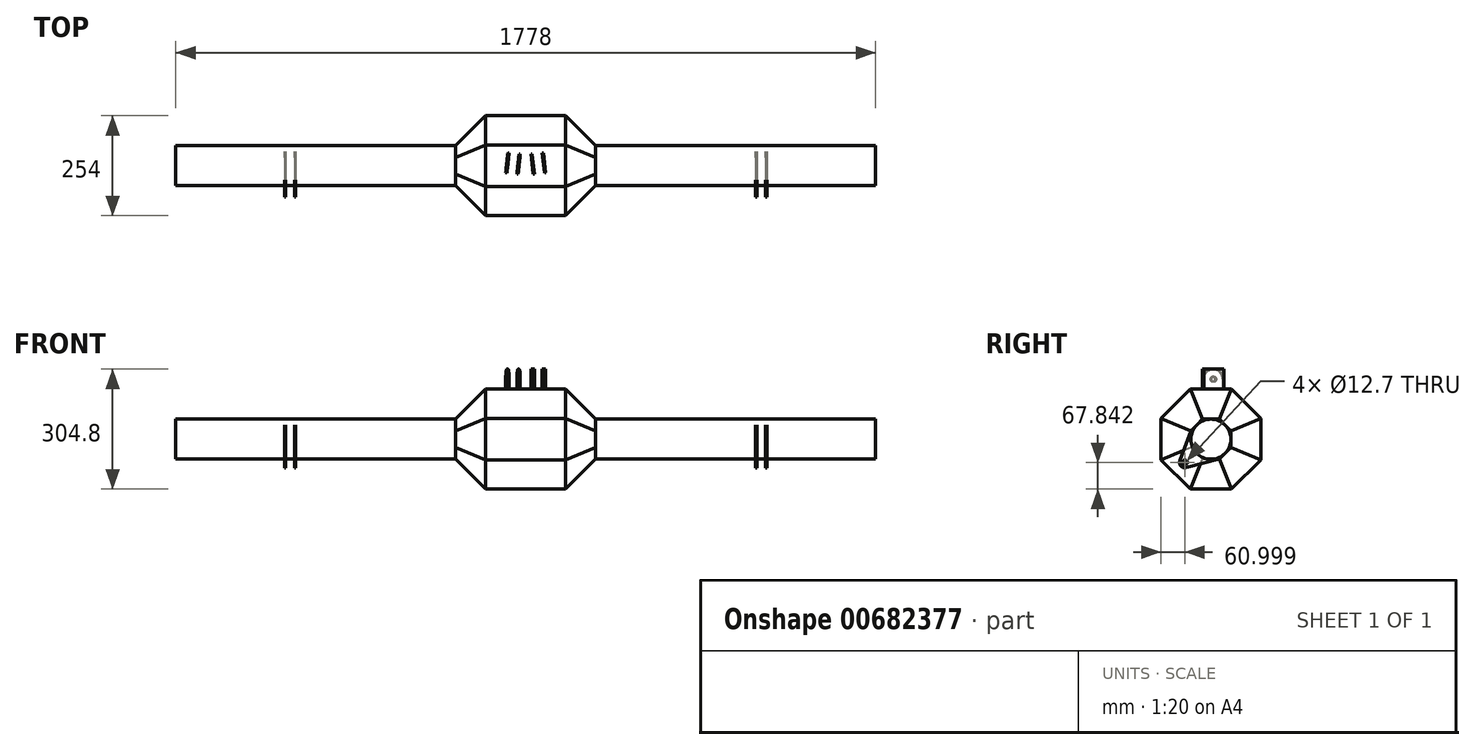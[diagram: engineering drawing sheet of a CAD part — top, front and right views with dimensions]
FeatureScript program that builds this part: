
annotation { "Feature Type Name" : "Feature", "Feature Type Description" : "" }
export const myFeature = defineFeature(function(context is Context, id is Id, definition is map)
    precondition{}
    {
        {
            var Q0;
            Q0=qCreatedBy(makeId("Right.planeOp"),FACE);
            var sketch = newSketch(context, id + "F0", { "sketchPlane" : qUnion([Q0])});
            skCircle(sketch, "E0", {"center": v(0, 0) * mm, "radius": 50.8 * mm});
            skSolve(sketch);
        }
        {
            var Q0;
            Q0=makeQuery(id+"F0.imprint","IMPRINT",FACE,{"disambiguationData":[TD([[makeQuery(id+"F0.imprint","IMPRINT",EDGE,{"derivedFrom":sQuery(id+"F0.wireOp",EDGE,"E0")}),1.0]])]});
            extrude(context, id + "F1", {"entities" : qUnion([Q0]), "endBound" : BoundingType.SYMMETRIC, "depth" : 1778 * mm, "offsetDistance" : 25.4 * mm});
        }
        {
            var Q0;
            Q0=qCreatedBy(makeId("Right.planeOp"),FACE);
            var sketch = newSketch(context, id + "F2", { "sketchPlane" : qUnion([Q0])});
            skCircle(sketch, "E1.cCircle", {"center": v(0, 0) * mm, "radius": 127 * mm, "construction": true});
            skLineSegment(sketch, "E1.0", {"start": v(52.6, 127) * mm, "end": v(127, 52.6) * mm});
            skLineSegment(sketch, "E1.1", {"start": v(127, 52.6) * mm, "end": v(127, -52.6) * mm});
            skLineSegment(sketch, "E1.2", {"start": v(127, -52.6) * mm, "end": v(52.6, -127) * mm});
            skLineSegment(sketch, "E1.3", {"start": v(52.6, -127) * mm, "end": v(-52.6, -127) * mm});
            skLineSegment(sketch, "E1.4", {"start": v(-52.6, -127) * mm, "end": v(-127, -52.6) * mm});
            skLineSegment(sketch, "E1.5", {"start": v(-127, -52.6) * mm, "end": v(-127, 52.6) * mm});
            skLineSegment(sketch, "E1.6", {"start": v(-127, 52.6) * mm, "end": v(-52.6, 127) * mm});
            skLineSegment(sketch, "E1.7", {"start": v(-52.6, 127) * mm, "end": v(52.6, 127) * mm});
            skPoint(sketch, "E1.0.midPoint", {"position": v(89.8, 89.8) * mm});
            skSolve(sketch);
        }
        {
            var Q0;
            Q0=makeQuery(id+"F2.imprint","IMPRINT",FACE,{"disambiguationData":[TD([[makeQuery(id+"F2.imprint","IMPRINT",EDGE,{"derivedFrom":sQuery(id+"F2.wireOp",EDGE,"E1.0")}),-1.0]])]});
            extrude(context, id + "F3", {"entities" : qUnion([Q0]), "operationType" : NewBodyOperationType.ADD, "endBound" : BoundingType.SYMMETRIC, "depth" : 355.6 * mm, "offsetDistance" : 25.4 * mm});
        }
        {
            var Q0;
            Q0=makeQuery(id+"F3.opExtrude","CAP_EDGE",EDGE,{"disambiguationData":[OSD([sQuery(id+"F2.wireOp",EDGE,"E1.5")])],"isStart":true});
            var Q1;
            Q1=makeQuery(id+"F3.opExtrude","CAP_EDGE",EDGE,{"disambiguationData":[OSD([sQuery(id+"F2.wireOp",EDGE,"E1.6")])],"isStart":true});
            var Q2;
            Q2=makeQuery(id+"F3.opExtrude","CAP_EDGE",EDGE,{"disambiguationData":[OSD([sQuery(id+"F2.wireOp",EDGE,"E1.7")])],"isStart":true});
            var Q3;
            Q3=makeQuery(id+"F3.opExtrude","CAP_EDGE",EDGE,{"disambiguationData":[OSD([sQuery(id+"F2.wireOp",EDGE,"E1.0")])],"isStart":true});
            var Q4;
            Q4=makeQuery(id+"F3.opExtrude","CAP_EDGE",EDGE,{"disambiguationData":[OSD([sQuery(id+"F2.wireOp",EDGE,"E1.1")])],"isStart":true});
            var Q5;
            Q5=makeQuery(id+"F3.opExtrude","CAP_EDGE",EDGE,{"disambiguationData":[OSD([sQuery(id+"F2.wireOp",EDGE,"E1.2")])],"isStart":true});
            var Q6;
            Q6=makeQuery(id+"F3.opExtrude","CAP_EDGE",EDGE,{"disambiguationData":[OSD([sQuery(id+"F2.wireOp",EDGE,"E1.3")])],"isStart":true});
            var Q7;
            Q7=makeQuery(id+"F3.opExtrude","CAP_EDGE",EDGE,{"disambiguationData":[OSD([sQuery(id+"F2.wireOp",EDGE,"E1.4")])],"isStart":true});
            chamfer(context, id + "F4", {"entities" : qUnion([Q0, Q1, Q2, Q3, Q4, Q5, Q6, Q7]), "width" : 76.2 * mm, "tangentPropagation" : true});
        }
        {
            var Q0;
            Q0=makeQuery(id+"F3.opExtrude","CAP_EDGE",EDGE,{"disambiguationData":[OSD([sQuery(id+"F2.wireOp",EDGE,"E1.0")])],"isStart":false});
            var Q1;
            Q1=makeQuery(id+"F3.opExtrude","CAP_EDGE",EDGE,{"disambiguationData":[OSD([sQuery(id+"F2.wireOp",EDGE,"E1.6")])],"isStart":false});
            var Q2;
            Q2=makeQuery(id+"F3.opExtrude","CAP_EDGE",EDGE,{"disambiguationData":[OSD([sQuery(id+"F2.wireOp",EDGE,"E1.7")])],"isStart":false});
            var Q3;
            Q3=makeQuery(id+"F3.opExtrude","CAP_EDGE",EDGE,{"disambiguationData":[OSD([sQuery(id+"F2.wireOp",EDGE,"E1.5")])],"isStart":false});
            var Q4;
            Q4=makeQuery(id+"F3.opExtrude","CAP_EDGE",EDGE,{"disambiguationData":[OSD([sQuery(id+"F2.wireOp",EDGE,"E1.4")])],"isStart":false});
            var Q5;
            Q5=makeQuery(id+"F3.opExtrude","CAP_EDGE",EDGE,{"disambiguationData":[OSD([sQuery(id+"F2.wireOp",EDGE,"E1.3")])],"isStart":false});
            var Q6;
            Q6=makeQuery(id+"F3.opExtrude","CAP_EDGE",EDGE,{"disambiguationData":[OSD([sQuery(id+"F2.wireOp",EDGE,"E1.2")])],"isStart":false});
            var Q7;
            Q7=makeQuery(id+"F3.opExtrude","CAP_EDGE",EDGE,{"disambiguationData":[OSD([sQuery(id+"F2.wireOp",EDGE,"E1.1")])],"isStart":false});
            chamfer(context, id + "F5", {"entities" : qUnion([Q0, Q1, Q2, Q3, Q4, Q5, Q6, Q7]), "width" : 76.2 * mm, "tangentPropagation" : true});
        }
        {
            var Q0;
            Q0=makeQuery(id+"F1.opExtrude","CAP_FACE",FACE,{"disambiguationData":[OSD([sQuery(id+"F0.wireOp",EDGE,"E0")])],"isStart":true});
            cPlane(context, id + "F6", {"entities" : qUnion([Q0]), "cplaneType" : CPlaneType.OFFSET, "offset" : 304.8 * mm, "oppositeDirection" : true, "width" : 152.4 * mm, "height" : 152.4 * mm});
        }
        {
            var Q0;
            Q0=qCreatedBy(id+"F6.planeOp",FACE);
            var sketch = newSketch(context, id + "F7", { "sketchPlane" : qUnion([Q0])});
            skCircle(sketch, "E2", {"center": v(66, -59.16) * mm, "radius": 6.35 * mm});
            skPoint(sketch, "E3", {"position": v(50.8, 21.04) * mm});
            skPoint(sketch, "E4", {"position": v(-21.04, -50.8) * mm});
            skLineSegment(sketch, "E5", {"start": v(62.22, -64.26) * mm, "end": v(66, -59.16) * mm});
            skLineSegment(sketch, "E6", {"start": v(69.78, -54.06) * mm, "end": v(66, -59.16) * mm});
            skCircle(sketch, "E7.0", {"center": v(0, 0) * mm, "radius": 50.8 * mm});
            skLineSegment(sketch, "E8", {"start": v(50.8, 21.04) * mm, "end": v(35.92, 35.92) * mm});
            skLineSegment(sketch, "E9", {"start": v(-21.04, -50.8) * mm, "end": v(-35.82, -36.03) * mm});
            skArc(sketch, "E10", {"start": v(62.57, -72.43) * mm, "mid": v(76.18, -68.34) * mm, "end": v(78.85, -54.38) * mm});
            skLineSegment(sketch, "E11", {"start": v(50.8, 21.04) * mm, "end": v(78.85, -54.38) * mm});
            skLineSegment(sketch, "E12", {"start": v(-21.04, -50.8) * mm, "end": v(62.57, -72.43) * mm});
            skSolve(sketch);
        }
        {
            var Q0;
            {var subQ0=sQuery(id+"F7.wireOp",EDGE,"E8");Q0=makeQuery(id+"F7.imprint","IMPRINT",FACE,{"disambiguationData":[TD([[makeQuery(id+"F7.imprint","IMPRINT",EDGE,{"derivedFrom":subQ0}),1.0]])]});}
            extrude(context, id + "F8", {"entities" : qUnion([Q0]), "depth" : 3.17 * mm, "offsetDistance" : 25.4 * mm});
        }
        {
            var Q0;
            Q0=makeQuery(id+"F8.opExtrude","SWEPT_BODY",BODY,{"disambiguationData":[OSD([sQuery(id+"F7.wireOp",EDGE,"E2"),sQuery(id+"F7.wireOp",EDGE,"E7.0"),sQuery(id+"F7.wireOp",EDGE,"E8"),sQuery(id+"F7.wireOp",EDGE,"E9"),sQuery(id+"F7.wireOp",EDGE,"E10"),sQuery(id+"F7.wireOp",EDGE,"E11"),sQuery(id+"F7.wireOp",EDGE,"E12")])]});
            var Q1;
            {var subQ0=sQuery(id+"F0.wireOp",EDGE,"E0");Q1=makeQuery(id+"F3.boolean.opBoolean","SPLIT",FACE,{"disambiguationData":[TD([makeQuery(id+"F1.opExtrude","CAP_FACE",FACE,{"disambiguationData":[OSD([subQ0])],"isStart":true})])],"derivedFrom":makeQuery(id+"F1.opExtrude","SWEPT_FACE",FACE,{"disambiguationData":[OSD([subQ0])]})});}
            transform(context, id + "F9", {"entities" : qUnion([Q0]), "transformType" : TransformType.TRANSLATION_DISTANCE, "transformDirection" : qUnion([Q1]), "distance" : 25.4 * mm, "makeCopy" : true});
        }
        {
            var Q0;
            Q0=makeQuery(id+"F1.opExtrude","CAP_FACE",FACE,{"disambiguationData":[OSD([sQuery(id+"F0.wireOp",EDGE,"E0")])],"isStart":true});
            var Q1;
            Q1=makeQuery(id+"F1.opExtrude","CAP_FACE",FACE,{"disambiguationData":[OSD([sQuery(id+"F0.wireOp",EDGE,"E0")])],"isStart":false});
            cPlane(context, id + "F10", {"entities" : qUnion([Q0, Q1]), "cplaneType" : CPlaneType.MID_PLANE, "offset" : 25.4 * mm, "width" : 152.4 * mm, "height" : 152.4 * mm});
        }
        {
            var Q0;
            Q0=makeQuery(id+"F8.opExtrude","SWEPT_BODY",BODY,{"disambiguationData":[OSD([sQuery(id+"F7.wireOp",EDGE,"E2"),sQuery(id+"F7.wireOp",EDGE,"E7.0"),sQuery(id+"F7.wireOp",EDGE,"E8"),sQuery(id+"F7.wireOp",EDGE,"E9"),sQuery(id+"F7.wireOp",EDGE,"E10"),sQuery(id+"F7.wireOp",EDGE,"E11"),sQuery(id+"F7.wireOp",EDGE,"E12")])]});
            var Q1;
            Q1=makeQuery(id+"F9.opPattern","COPY",BODY,{"derivedFrom":makeQuery(id+"F8.opExtrude","SWEPT_BODY",BODY,{"disambiguationData":[OSD([sQuery(id+"F7.wireOp",EDGE,"E2"),sQuery(id+"F7.wireOp",EDGE,"E7.0"),sQuery(id+"F7.wireOp",EDGE,"E8"),sQuery(id+"F7.wireOp",EDGE,"E9"),sQuery(id+"F7.wireOp",EDGE,"E10"),sQuery(id+"F7.wireOp",EDGE,"E11"),sQuery(id+"F7.wireOp",EDGE,"E12")])]}),"instanceName":"1"});
            var Q2;
            Q2=qCreatedBy(id+"F10.planeOp",FACE);
            mirror(context, id + "F11", {"operationType" : NewBodyOperationType.ADD, "entities" : qUnion([Q0, Q1]), "mirrorPlane" : qUnion([Q2])});
        }
        {
            var Q0;
            Q0=makeQuery(id+"F3.opExtrude","SWEPT_FACE",FACE,{"disambiguationData":[OSD([sQuery(id+"F2.wireOp",EDGE,"E1.7")])]});
            var sketch = newSketch(context, id + "F12", { "sketchPlane" : qUnion([Q0])});
            skLineSegment(sketch, "E13", {"start": v(-50.68, -17.7) * mm, "end": v(-45.23, 32.81) * mm});
            skLineSegment(sketch, "E14", {"start": v(-42.08, 32.47) * mm, "end": v(-47.53, -18.03) * mm});
            skPoint(sketch, "E15.orphan", {"position": v(-54.45, -52.6) * mm});
            skPoint(sketch, "E16.orphan", {"position": v(-54.45, -52.26) * mm});
            skLineSegment(sketch, "E17", {"start": v(-16.82, 29.75) * mm, "end": v(-22.27, -20.76) * mm});
            skLineSegment(sketch, "E18.0", {"start": v(-13.67, 29.4) * mm, "end": v(-19.12, -21.1) * mm});
            skLineSegment(sketch, "E19", {"start": v(-50.68, -17.7) * mm, "end": v(-19.12, -21.1) * mm});
            skLineSegment(sketch, "E20", {"start": v(-45.23, 32.81) * mm, "end": v(-13.67, 29.4) * mm});
            skLineSegment(sketch, "E21", {"start": v(0, 0) * mm, "end": v(0, 70.8) * mm, "construction": true});
            skLineSegment(sketch, "E22.MirrorCS", {"start": v(50.68, -17.7) * mm, "end": v(45.23, 32.81) * mm});
            skLineSegment(sketch, "E23.MirrorCS", {"start": v(42.08, 32.47) * mm, "end": v(47.53, -18.03) * mm});
            skLineSegment(sketch, "E24.MirrorCS", {"start": v(45.23, 32.81) * mm, "end": v(13.67, 29.4) * mm});
            skLineSegment(sketch, "E25.MirrorCS", {"start": v(50.68, -17.7) * mm, "end": v(19.12, -21.1) * mm});
            skLineSegment(sketch, "E26.MirrorCS", {"start": v(13.67, 29.4) * mm, "end": v(19.12, -21.1) * mm});
            skLineSegment(sketch, "E27.MirrorCS", {"start": v(16.82, 29.75) * mm, "end": v(22.27, -20.76) * mm});
            skSolve(sketch);
        }
        {
            var Q0;
            {var subQ0=sQuery(id+"F12.wireOp",EDGE,"E13");Q0=makeQuery(id+"F12.imprint","IMPRINT",FACE,{"disambiguationData":[TD([[makeQuery(id+"F12.imprint","IMPRINT",EDGE,{"derivedFrom":subQ0}),-1.0]])]});}
            var Q1;
            {var subQ0=sQuery(id+"F12.wireOp",EDGE,"E17");Q1=makeQuery(id+"F12.imprint","IMPRINT",FACE,{"disambiguationData":[TD([[makeQuery(id+"F12.imprint","IMPRINT",EDGE,{"derivedFrom":subQ0}),1.0]])]});}
            var Q2;
            {var subQ0=sQuery(id+"F12.wireOp",EDGE,"E26.MirrorCS");Q2=makeQuery(id+"F12.imprint","IMPRINT",FACE,{"disambiguationData":[TD([[makeQuery(id+"F12.imprint","IMPRINT",EDGE,{"derivedFrom":subQ0}),1.0]])]});}
            var Q3;
            {var subQ0=sQuery(id+"F12.wireOp",EDGE,"E22.MirrorCS");Q3=makeQuery(id+"F12.imprint","IMPRINT",FACE,{"disambiguationData":[TD([[makeQuery(id+"F12.imprint","IMPRINT",EDGE,{"derivedFrom":subQ0}),1.0]])]});}
            extrude(context, id + "F13", {"entities" : qUnion([Q0, Q1, Q2, Q3]), "operationType" : NewBodyOperationType.ADD, "depth" : 50.8 * mm, "offsetDistance" : 25.4 * mm});
        }
        {
            var Q0;
            Q0=makeQuery(id+"F13.opExtrude","SWEPT_FACE",FACE,{"disambiguationData":[OSD([sQuery(id+"F12.wireOp",EDGE,"E13")])]});
            var sketch = newSketch(context, id + "F14", { "sketchPlane" : qUnion([Q0])});
            skArc(sketch, "E28", {"start": v(23.03, 152.4) * mm, "mid": v(-2.37, 177.8) * mm, "end": v(-27.77, 152.4) * mm});
            skSolve(sketch);
        }
        {
            var Q0;
            {var subQ0=sQuery(id+"F14.wireOp",EDGE,"E28");var subQ1=sQuery(id+"F12.wireOp",EDGE,"E13");var subQ4=makeQuery(id+"F13.opExtrude","CAP_EDGE",EDGE,{"disambiguationData":[OSD([subQ1])],"isStart":false});var subQ5=makeQuery(id+"F14.imprint","INTERSECT",VERTEX,{"derivedFrom":[subQ4,subQ0]});Q0=makeQuery(id+"F14.imprint","IMPRINT",FACE,{"disambiguationData":[TD([[makeQuery(id+"F14.imprint","IMPRINT",EDGE,{"disambiguationData":[TD([[subQ5,-1.0]])],"derivedFrom":subQ0}),-1.0]])]});}
            var Q1;
            {var subQ0=sQuery(id+"F14.wireOp",EDGE,"E28");var subQ1=sQuery(id+"F12.wireOp",EDGE,"E13");var subQ4=makeQuery(id+"F13.opExtrude","CAP_EDGE",EDGE,{"disambiguationData":[OSD([subQ1])],"isStart":false});var subQ5=makeQuery(id+"F14.imprint","INTERSECT",VERTEX,{"derivedFrom":[subQ4,subQ0]});Q1=makeQuery(id+"F14.imprint","IMPRINT",FACE,{"disambiguationData":[TD([[makeQuery(id+"F14.imprint","IMPRINT",EDGE,{"disambiguationData":[TD([[subQ5,1.0]])],"derivedFrom":subQ0}),-1.0]])]});}
            extrude(context, id + "F15", {"entities" : qUnion([Q0, Q1]), "operationType" : NewBodyOperationType.REMOVE, "oppositeDirection" : true, "depth" : 33.53 * mm, "offsetDistance" : 25.4 * mm});
        }
        {
            var Q0;
            Q0=makeQuery(id+"F13.opExtrude","SWEPT_FACE",FACE,{"disambiguationData":[OSD([sQuery(id+"F12.wireOp",EDGE,"E13")])]});
            var sketch = newSketch(context, id + "F16", { "sketchPlane" : qUnion([Q0])});
            skCircle(sketch, "E29", {"center": v(-2.37, 152.4) * mm, "radius": 6.35 * mm});
            skSolve(sketch);
        }
        {
            var Q0;
            Q0=makeQuery(id+"F16.imprint","IMPRINT",FACE,{"disambiguationData":[TD([[makeQuery(id+"F16.imprint","IMPRINT",EDGE,{"derivedFrom":sQuery(id+"F16.wireOp",EDGE,"E29")}),1.0]])]});
            extrude(context, id + "F17", {"entities" : qUnion([Q0]), "operationType" : NewBodyOperationType.REMOVE, "oppositeDirection" : true, "depth" : 46.48 * mm, "offsetDistance" : 25.4 * mm});
        }
    });
